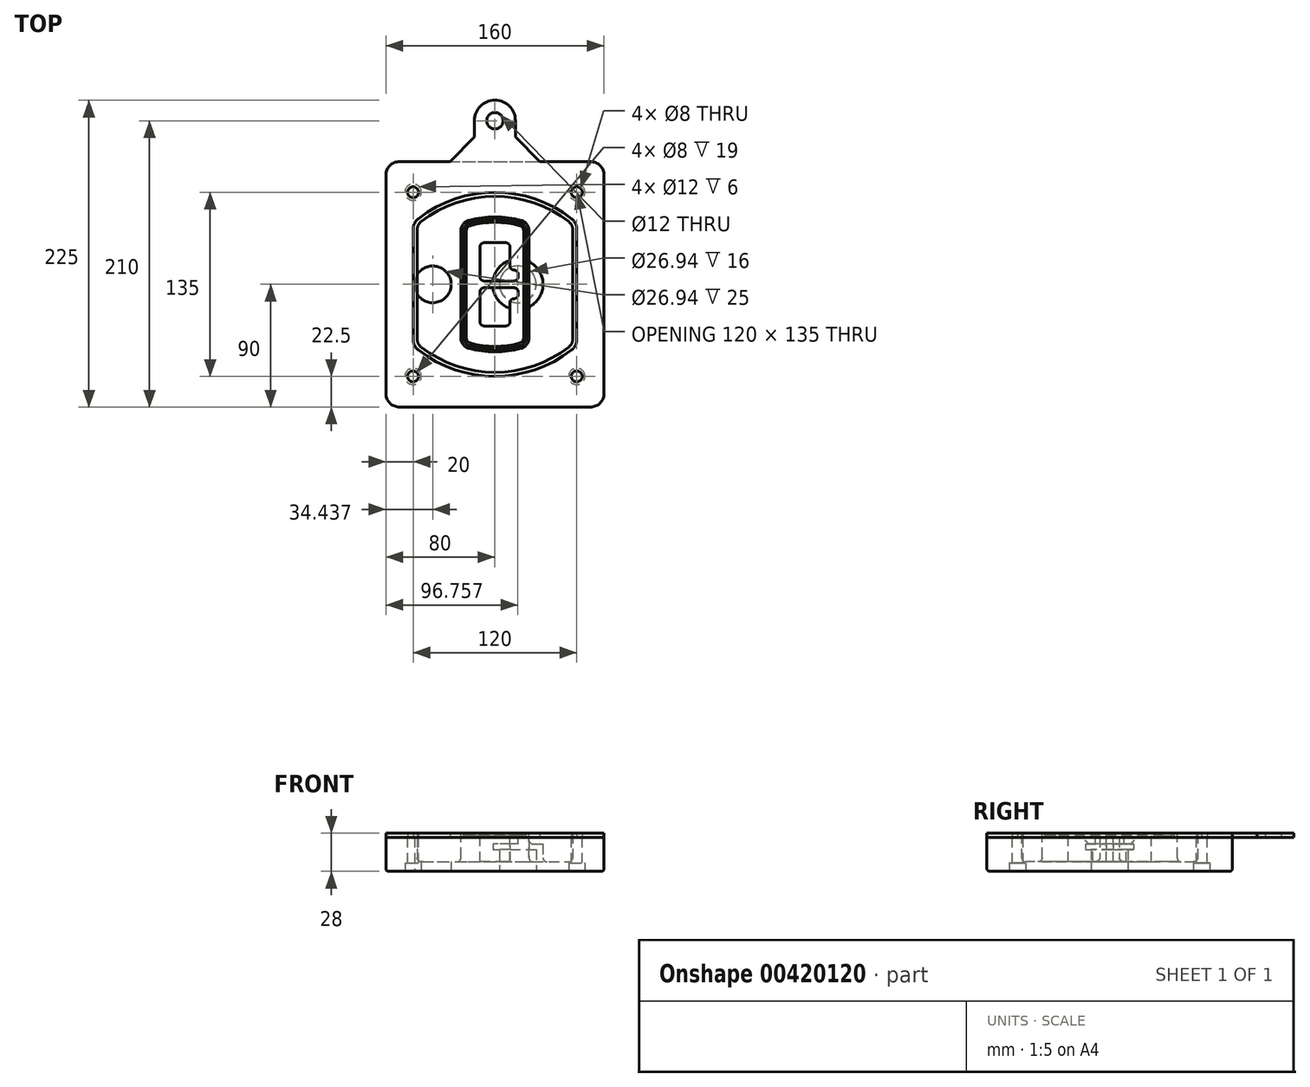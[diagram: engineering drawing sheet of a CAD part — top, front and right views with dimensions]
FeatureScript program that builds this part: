
annotation { "Feature Type Name" : "Feature", "Feature Type Description" : "" }
export const myFeature = defineFeature(function(context is Context, id is Id, definition is map)
    precondition{}
    {
        {
            var Q0;
            Q0=qCreatedBy(makeId("Top.planeOp"),FACE);
            var sketch = newSketch(context, id + "F0", { "sketchPlane" : qUnion([Q0])});
            skPoint(sketch, "E0.rect.middle", {"position": v(0, 0) * mm});
            skLineSegment(sketch, "E1.bottom", {"start": v(-70, -90) * mm, "end": v(70, -90) * mm});
            skLineSegment(sketch, "E1.top", {"start": v(-70, 90) * mm, "end": v(70, 90) * mm});
            skLineSegment(sketch, "E1.left", {"start": v(-80, -80) * mm, "end": v(-80, 80) * mm});
            skLineSegment(sketch, "E1.right", {"start": v(80, -80) * mm, "end": v(80, 80) * mm});
            skLineSegment(sketch, "E2", {"start": v(-80, 90) * mm, "end": v(80, -90) * mm, "construction": true});
            skLineSegment(sketch, "E3", {"start": v(80, 90) * mm, "end": v(-80, -90) * mm, "construction": true});
            skCircle(sketch, "E4", {"center": v(-60, 67.5) * mm, "radius": 4 * mm});
            skCircle(sketch, "E5", {"center": v(60, 67.5) * mm, "radius": 4 * mm});
            skCircle(sketch, "E6", {"center": v(60, -67.5) * mm, "radius": 4 * mm});
            skCircle(sketch, "E7", {"center": v(-60, -67.5) * mm, "radius": 4 * mm});
            skLineSegment(sketch, "E8", {"start": v(-60, 67.5) * mm, "end": v(60, 67.5) * mm, "construction": true});
            skLineSegment(sketch, "E9", {"start": v(60, 67.5) * mm, "end": v(60, -67.5) * mm, "construction": true});
            skLineSegment(sketch, "E10", {"start": v(60, -67.5) * mm, "end": v(-60, -67.5) * mm, "construction": true});
            skLineSegment(sketch, "E11", {"start": v(-60, -67.5) * mm, "end": v(-60, 67.5) * mm, "construction": true});
            skLineSegment(sketch, "E12", {"start": v(-60, 40.3) * mm, "end": v(-60, -40.3) * mm});
            skLineSegment(sketch, "E13", {"start": v(60, 40.3) * mm, "end": v(60, -40.3) * mm});
            skArc(sketch, "E14", {"start": v(56.15, 48.18) * mm, "mid": v(0, 67.5) * mm, "end": v(-56.15, 48.18) * mm});
            skArc(sketch, "E15", {"start": v(-56.15, -48.18) * mm, "mid": v(0, -67.5) * mm, "end": v(56.15, -48.18) * mm});
            skLineSegment(sketch, "E16", {"start": v(-60, 0) * mm, "end": v(60, 0) * mm, "construction": true});
            skPoint(sketch, "E17.visualSharp", {"position": v(-60, -45) * mm});
            skArc(sketch, "E17.filletArc", {"start": v(-60, -40.3) * mm, "mid": v(-58.99, -44.68) * mm, "end": v(-56.15, -48.18) * mm});
            skPoint(sketch, "E18.visualSharp", {"position": v(-60, 45) * mm});
            skArc(sketch, "E18.filletArc", {"start": v(-56.15, 48.18) * mm, "mid": v(-58.99, 44.68) * mm, "end": v(-60, 40.3) * mm});
            skPoint(sketch, "E19.visualSharp", {"position": v(60, 45) * mm});
            skArc(sketch, "E19.filletArc", {"start": v(60, 40.3) * mm, "mid": v(58.99, 44.68) * mm, "end": v(56.15, 48.18) * mm});
            skPoint(sketch, "E20.visualSharp", {"position": v(60, -45) * mm});
            skArc(sketch, "E20.filletArc", {"start": v(56.15, -48.18) * mm, "mid": v(58.99, -44.68) * mm, "end": v(60, -40.3) * mm});
            skPoint(sketch, "E21.visualSharp", {"position": v(-80, 90) * mm});
            skArc(sketch, "E21.filletArc", {"start": v(-70, 90) * mm, "mid": v(-77.07, 87.07) * mm, "end": v(-80, 80) * mm});
            skPoint(sketch, "E22.visualSharp", {"position": v(80, 90) * mm});
            skArc(sketch, "E22.filletArc", {"start": v(80, 80) * mm, "mid": v(77.07, 87.07) * mm, "end": v(70, 90) * mm});
            skPoint(sketch, "E23.visualSharp", {"position": v(80, -90) * mm});
            skArc(sketch, "E23.filletArc", {"start": v(70, -90) * mm, "mid": v(77.07, -87.07) * mm, "end": v(80, -80) * mm});
            skPoint(sketch, "E24.visualSharp", {"position": v(-80, -90) * mm});
            skArc(sketch, "E24.filletArc", {"start": v(-80, -80) * mm, "mid": v(-77.07, -87.07) * mm, "end": v(-70, -90) * mm});
            skArc(sketch, "E25.0", {"start": v(57, 40.3) * mm, "mid": v(56.3, 43.36) * mm, "end": v(54.3, 45.81) * mm});
            skLineSegment(sketch, "E25.1", {"start": v(57, 40.3) * mm, "end": v(57, -40.3) * mm});
            skArc(sketch, "E25.2", {"start": v(54.3, -45.81) * mm, "mid": v(56.3, -43.36) * mm, "end": v(57, -40.3) * mm});
            skArc(sketch, "E25.3", {"start": v(-54.3, -45.81) * mm, "mid": v(0, -64.5) * mm, "end": v(54.3, -45.81) * mm});
            skArc(sketch, "E25.4", {"start": v(-57, -40.3) * mm, "mid": v(-56.3, -43.36) * mm, "end": v(-54.3, -45.81) * mm});
            skArc(sketch, "E25.5", {"start": v(54.3, 45.81) * mm, "mid": v(0, 64.5) * mm, "end": v(-54.3, 45.81) * mm});
            skLineSegment(sketch, "E25.6", {"start": v(-57, 40.3) * mm, "end": v(-57, -40.3) * mm});
            skArc(sketch, "E25.7", {"start": v(-54.3, 45.81) * mm, "mid": v(-56.3, 43.36) * mm, "end": v(-57, 40.3) * mm});
            skArc(sketch, "E26.0", {"start": v(-58.62, 51.33) * mm, "mid": v(-62.58, 46.43) * mm, "end": v(-64, 40.3) * mm});
            skArc(sketch, "E26.1", {"start": v(58.62, 51.33) * mm, "mid": v(0, 71.5) * mm, "end": v(-58.62, 51.33) * mm});
            skArc(sketch, "E26.2", {"start": v(64, 40.3) * mm, "mid": v(62.58, 46.43) * mm, "end": v(58.62, 51.33) * mm});
            skLineSegment(sketch, "E26.3", {"start": v(64, 40.3) * mm, "end": v(64, -40.3) * mm});
            skArc(sketch, "E26.4", {"start": v(58.62, -51.33) * mm, "mid": v(62.58, -46.43) * mm, "end": v(64, -40.3) * mm});
            skLineSegment(sketch, "E26.5", {"start": v(-64, 40.3) * mm, "end": v(-64, -40.3) * mm});
            skArc(sketch, "E26.6", {"start": v(-58.62, -51.33) * mm, "mid": v(0, -71.5) * mm, "end": v(58.62, -51.33) * mm});
            skArc(sketch, "E26.7", {"start": v(-64, -40.3) * mm, "mid": v(-62.58, -46.43) * mm, "end": v(-58.62, -51.33) * mm});
            skSolve(sketch);
        }
        {
            var Q0;
            Q0=makeQuery(id+"F0.imprint","IMPRINT",FACE,{"disambiguationData":[TD([[makeQuery(id+"F0.imprint","IMPRINT",EDGE,{"derivedFrom":sQuery(id+"F0.wireOp",EDGE,"E1.bottom")}),1.0]])]});
            var Q1;
            Q1=makeQuery(id+"F0.imprint","IMPRINT",FACE,{"disambiguationData":[TD([[makeQuery(id+"F0.imprint","IMPRINT",EDGE,{"derivedFrom":sQuery(id+"F0.wireOp",EDGE,"E12")}),1.0]])]});
            var Q2;
            Q2=makeQuery(id+"F0.imprint","IMPRINT",FACE,{"disambiguationData":[TD([[makeQuery(id+"F0.imprint","IMPRINT",EDGE,{"derivedFrom":sQuery(id+"F0.wireOp",EDGE,"E25.0")}),1.0]])]});
            var Q3;
            Q3=makeQuery(id+"F0.imprint","IMPRINT",FACE,{"disambiguationData":[TD([[makeQuery(id+"F0.imprint","IMPRINT",EDGE,{"derivedFrom":sQuery(id+"F0.wireOp",EDGE,"E12")}),-1.0]])]});
            extrude(context, id + "F1", {"entities" : qUnion([Q0, Q1, Q2, Q3]), "oppositeDirection" : true, "depth" : 25 * mm});
        }
        {
            var Q0;
            Q0=makeQuery(id+"F0.imprint","IMPRINT",FACE,{"disambiguationData":[TD([[makeQuery(id+"F0.imprint","IMPRINT",EDGE,{"derivedFrom":sQuery(id+"F0.wireOp",EDGE,"E12")}),1.0]])]});
            extrude(context, id + "F2", {"entities" : qUnion([Q0]), "operationType" : NewBodyOperationType.ADD, "depth" : 3 * mm});
        }
        {
            var Q0;
            Q0=makeQuery(id+"F0.imprint","IMPRINT",FACE,{"disambiguationData":[TD([[makeQuery(id+"F0.imprint","IMPRINT",EDGE,{"derivedFrom":sQuery(id+"F0.wireOp",EDGE,"E25.0")}),1.0]])]});
            extrude(context, id + "F3", {"entities" : qUnion([Q0]), "operationType" : NewBodyOperationType.REMOVE, "oppositeDirection" : true, "depth" : 18 * mm});
        }
        {
            var Q0;
            Q0=makeQuery(id+"F2.opExtrude","CAP_FACE",FACE,{"disambiguationData":[OSD([sQuery(id+"F0.wireOp",EDGE,"E12"),sQuery(id+"F0.wireOp",EDGE,"E13"),sQuery(id+"F0.wireOp",EDGE,"E14"),sQuery(id+"F0.wireOp",EDGE,"E15"),sQuery(id+"F0.wireOp",EDGE,"E17.filletArc"),sQuery(id+"F0.wireOp",EDGE,"E18.filletArc"),sQuery(id+"F0.wireOp",EDGE,"E19.filletArc"),sQuery(id+"F0.wireOp",EDGE,"E20.filletArc"),sQuery(id+"F0.wireOp",EDGE,"E25.0"),sQuery(id+"F0.wireOp",EDGE,"E25.1"),sQuery(id+"F0.wireOp",EDGE,"E25.2"),sQuery(id+"F0.wireOp",EDGE,"E25.3"),sQuery(id+"F0.wireOp",EDGE,"E25.4"),sQuery(id+"F0.wireOp",EDGE,"E25.5"),sQuery(id+"F0.wireOp",EDGE,"E25.6"),sQuery(id+"F0.wireOp",EDGE,"E25.7")])],"isStart":false});
            var sketch = newSketch(context, id + "F4", { "sketchPlane" : qUnion([Q0])});
            skArc(sketch, "E27.0", {"start": v(-19.08, -46.97) * mm, "mid": v(0, -49.5) * mm, "end": v(19.08, -46.97) * mm});
            skArc(sketch, "E28.0", {"start": v(19.08, 46.97) * mm, "mid": v(0, 49.5) * mm, "end": v(-19.08, 46.97) * mm});
            skLineSegment(sketch, "E29", {"start": v(-25, 39.25) * mm, "end": v(-25, -39.25) * mm});
            skLineSegment(sketch, "E30", {"start": v(25, 39.25) * mm, "end": v(25, -39.25) * mm});
            skLineSegment(sketch, "E31", {"start": v(-25, 45.1) * mm, "end": v(25, 45.1) * mm, "construction": true});
            skLineSegment(sketch, "E32", {"start": v(-25, -45.1) * mm, "end": v(25, -45.1) * mm, "construction": true});
            skPoint(sketch, "E33.visualSharp", {"position": v(-25, 45.1) * mm});
            skArc(sketch, "E33.filletArc", {"start": v(-19.08, 46.97) * mm, "mid": v(-23.35, 44.11) * mm, "end": v(-25, 39.25) * mm});
            skPoint(sketch, "E34.visualSharp", {"position": v(25, 45.1) * mm});
            skArc(sketch, "E34.filletArc", {"start": v(25, 39.25) * mm, "mid": v(23.35, 44.11) * mm, "end": v(19.08, 46.97) * mm});
            skPoint(sketch, "E35.visualSharp", {"position": v(25, -45.1) * mm});
            skArc(sketch, "E35.filletArc", {"start": v(19.08, -46.97) * mm, "mid": v(23.35, -44.11) * mm, "end": v(25, -39.25) * mm});
            skPoint(sketch, "E36.visualSharp", {"position": v(-25, -45.1) * mm});
            skArc(sketch, "E36.filletArc", {"start": v(-25, -39.25) * mm, "mid": v(-23.35, -44.11) * mm, "end": v(-19.08, -46.97) * mm});
            skArc(sketch, "E37.0", {"start": v(54.3, 45.81) * mm, "mid": v(0, 64.5) * mm, "end": v(-54.3, 45.81) * mm});
            skArc(sketch, "E37.1", {"start": v(-54.3, 45.81) * mm, "mid": v(-56.3, 43.36) * mm, "end": v(-57, 40.3) * mm});
            skLineSegment(sketch, "E37.2", {"start": v(-57, 40.3) * mm, "end": v(-57, -40.3) * mm});
            skArc(sketch, "E37.3", {"start": v(-57, -40.3) * mm, "mid": v(-56.3, -43.36) * mm, "end": v(-54.3, -45.81) * mm});
            skArc(sketch, "E37.4", {"start": v(-54.3, -45.81) * mm, "mid": v(0, -64.5) * mm, "end": v(54.3, -45.81) * mm});
            skArc(sketch, "E37.5", {"start": v(54.3, -45.81) * mm, "mid": v(56.3, -43.36) * mm, "end": v(57, -40.3) * mm});
            skLineSegment(sketch, "E37.6", {"start": v(57, 40.3) * mm, "end": v(57, -40.3) * mm});
            skArc(sketch, "E37.7", {"start": v(57, 40.3) * mm, "mid": v(56.3, 43.36) * mm, "end": v(54.3, 45.81) * mm});
            skLineSegment(sketch, "E38.0", {"start": v(23, 39.25) * mm, "end": v(23, -39.25) * mm});
            skArc(sketch, "E38.1", {"start": v(18.56, -45.04) * mm, "mid": v(21.76, -42.9) * mm, "end": v(23, -39.25) * mm});
            skArc(sketch, "E38.2", {"start": v(-18.56, -45.04) * mm, "mid": v(0, -47.5) * mm, "end": v(18.56, -45.04) * mm});
            skArc(sketch, "E38.3", {"start": v(-23, -39.25) * mm, "mid": v(-21.76, -42.9) * mm, "end": v(-18.56, -45.04) * mm});
            skLineSegment(sketch, "E38.4", {"start": v(-23, 39.25) * mm, "end": v(-23, -39.25) * mm});
            skArc(sketch, "E38.5", {"start": v(23, 39.25) * mm, "mid": v(21.76, 42.9) * mm, "end": v(18.56, 45.04) * mm});
            skArc(sketch, "E38.6", {"start": v(-18.56, 45.04) * mm, "mid": v(-21.76, 42.9) * mm, "end": v(-23, 39.25) * mm});
            skArc(sketch, "E38.7", {"start": v(18.56, 45.04) * mm, "mid": v(0, 47.5) * mm, "end": v(-18.56, 45.04) * mm});
            skArc(sketch, "E39.0", {"start": v(21, 39.25) * mm, "mid": v(20.18, 41.68) * mm, "end": v(18.04, 43.1) * mm});
            skLineSegment(sketch, "E39.1", {"start": v(21, 39.25) * mm, "end": v(21, -39.25) * mm});
            skArc(sketch, "E39.2", {"start": v(18.04, -43.1) * mm, "mid": v(20.18, -41.68) * mm, "end": v(21, -39.25) * mm});
            skArc(sketch, "E39.3", {"start": v(-18.04, -43.1) * mm, "mid": v(0, -45.5) * mm, "end": v(18.04, -43.1) * mm});
            skArc(sketch, "E39.4", {"start": v(-21, -39.25) * mm, "mid": v(-20.18, -41.68) * mm, "end": v(-18.04, -43.1) * mm});
            skArc(sketch, "E39.5", {"start": v(18.04, 43.1) * mm, "mid": v(0, 45.5) * mm, "end": v(-18.04, 43.1) * mm});
            skLineSegment(sketch, "E39.6", {"start": v(-21, 39.25) * mm, "end": v(-21, -39.25) * mm});
            skArc(sketch, "E39.7", {"start": v(-18.04, 43.1) * mm, "mid": v(-20.18, 41.68) * mm, "end": v(-21, 39.25) * mm});
            skLineSegment(sketch, "E40", {"start": v(-25, 0) * mm, "end": v(25, 0) * mm, "construction": true});
            skLineSegment(sketch, "E41", {"start": v(-11, 5.5) * mm, "end": v(-11, 27.5) * mm});
            skLineSegment(sketch, "E42", {"start": v(-8, 30.5) * mm, "end": v(8, 30.5) * mm});
            skLineSegment(sketch, "E43", {"start": v(11, 27.5) * mm, "end": v(11, 13.5) * mm});
            skLineSegment(sketch, "E44", {"start": v(14, 10.5) * mm, "end": v(14, 10.5) * mm});
            skLineSegment(sketch, "E45", {"start": v(17, 7.5) * mm, "end": v(17, 5.5) * mm});
            skLineSegment(sketch, "E46", {"start": v(14, 2.5) * mm, "end": v(-8, 2.5) * mm});
            skPoint(sketch, "E47.visualSharp", {"position": v(-11, 30.5) * mm});
            skArc(sketch, "E47.filletArc", {"start": v(-8, 30.5) * mm, "mid": v(-10.12, 29.62) * mm, "end": v(-11, 27.5) * mm});
            skPoint(sketch, "E48.visualSharp", {"position": v(11, 30.5) * mm});
            skArc(sketch, "E48.filletArc", {"start": v(11, 27.5) * mm, "mid": v(10.12, 29.62) * mm, "end": v(8, 30.5) * mm});
            skPoint(sketch, "E49.visualSharp", {"position": v(11, 10.5) * mm});
            skArc(sketch, "E49.filletArc", {"start": v(11, 13.5) * mm, "mid": v(11.88, 11.38) * mm, "end": v(14, 10.5) * mm});
            skPoint(sketch, "E50.visualSharp", {"position": v(17, 10.5) * mm});
            skArc(sketch, "E50.filletArc", {"start": v(17, 7.5) * mm, "mid": v(16.12, 9.62) * mm, "end": v(14, 10.5) * mm});
            skPoint(sketch, "E51.visualSharp", {"position": v(17, 2.5) * mm});
            skArc(sketch, "E51.filletArc", {"start": v(14, 2.5) * mm, "mid": v(16.12, 3.38) * mm, "end": v(17, 5.5) * mm});
            skPoint(sketch, "E52.visualSharp", {"position": v(-11, 2.5) * mm});
            skArc(sketch, "E52.filletArc", {"start": v(-11, 5.5) * mm, "mid": v(-10.12, 3.38) * mm, "end": v(-8, 2.5) * mm});
            skLineSegment(sketch, "E53.0.MirrorCS", {"start": v(14, -2.5) * mm, "end": v(-8, -2.5) * mm});
            skArc(sketch, "E54.0.MirrorCS", {"start": v(-11, -5.5) * mm, "mid": v(-10.12, -3.38) * mm, "end": v(-8, -2.5) * mm});
            skLineSegment(sketch, "E55.0.MirrorCS", {"start": v(-11, -5.5) * mm, "end": v(-11, -27.5) * mm});
            skArc(sketch, "E56.0.MirrorCS", {"start": v(-8, -30.5) * mm, "mid": v(-10.12, -29.62) * mm, "end": v(-11, -27.5) * mm});
            skLineSegment(sketch, "E57.0.MirrorCS", {"start": v(-8, -30.5) * mm, "end": v(8, -30.5) * mm});
            skArc(sketch, "E58.0.MirrorCS", {"start": v(11, -27.5) * mm, "mid": v(10.12, -29.62) * mm, "end": v(8, -30.5) * mm});
            skLineSegment(sketch, "E59.0.MirrorCS", {"start": v(11, -27.5) * mm, "end": v(11, -13.5) * mm});
            skArc(sketch, "E60.0.MirrorCS", {"start": v(11, -13.5) * mm, "mid": v(11.88, -11.38) * mm, "end": v(14, -10.5) * mm});
            skArc(sketch, "E61.0.MirrorCS", {"start": v(17, -7.5) * mm, "mid": v(16.12, -9.62) * mm, "end": v(14, -10.5) * mm});
            skLineSegment(sketch, "E62.0.MirrorCS", {"start": v(17, -7.5) * mm, "end": v(17, -5.5) * mm});
            skArc(sketch, "E63.0.MirrorCS", {"start": v(14, -2.5) * mm, "mid": v(16.12, -3.38) * mm, "end": v(17, -5.5) * mm});
            skSolve(sketch);
        }
        {
            var Q0;
            Q0=makeQuery(id+"F4.imprint","IMPRINT",FACE,{"disambiguationData":[TD([[makeQuery(id+"F4.imprint","IMPRINT",EDGE,{"derivedFrom":sQuery(id+"F4.wireOp",EDGE,"E27.0")}),1.0]])]});
            var Q1;
            Q1=makeQuery(id+"F4.imprint","IMPRINT",FACE,{"disambiguationData":[TD([[makeQuery(id+"F4.imprint","IMPRINT",EDGE,{"derivedFrom":sQuery(id+"F4.wireOp",EDGE,"E38.0")}),-1.0]])]});
            var Q2;
            Q2=makeQuery(id+"F4.imprint","IMPRINT",FACE,{"disambiguationData":[TD([[makeQuery(id+"F4.imprint","IMPRINT",EDGE,{"derivedFrom":sQuery(id+"F4.wireOp",EDGE,"E39.0")}),1.0]])]});
            extrude(context, id + "F5", {"entities" : qUnion([Q0, Q1, Q2]), "operationType" : NewBodyOperationType.ADD, "endBound" : BoundingType.UP_TO_NEXT, "oppositeDirection" : true, "depth" : 25 * mm});
        }
        {
            var Q0;
            Q0=makeQuery(id+"F4.imprint","IMPRINT",FACE,{"disambiguationData":[TD([[makeQuery(id+"F4.imprint","IMPRINT",EDGE,{"derivedFrom":sQuery(id+"F4.wireOp",EDGE,"E38.0")}),-1.0]])]});
            extrude(context, id + "F6", {"entities" : qUnion([Q0]), "operationType" : NewBodyOperationType.REMOVE, "oppositeDirection" : true, "depth" : 2 * mm});
        }
        {
            var Q0;
            Q0=makeQuery(id+"F1.opExtrude","CAP_FACE",FACE,{"disambiguationData":[OSD([sQuery(id+"F0.wireOp",EDGE,"E1.bottom"),sQuery(id+"F0.wireOp",EDGE,"E1.top"),sQuery(id+"F0.wireOp",EDGE,"E1.left"),sQuery(id+"F0.wireOp",EDGE,"E1.right"),sQuery(id+"F0.wireOp",EDGE,"E4"),sQuery(id+"F0.wireOp",EDGE,"E5"),sQuery(id+"F0.wireOp",EDGE,"E6"),sQuery(id+"F0.wireOp",EDGE,"E7"),sQuery(id+"F0.wireOp",EDGE,"E21.filletArc"),sQuery(id+"F0.wireOp",EDGE,"E22.filletArc"),sQuery(id+"F0.wireOp",EDGE,"E23.filletArc"),sQuery(id+"F0.wireOp",EDGE,"E24.filletArc")])],"isStart":false});
            var sketch = newSketch(context, id + "F7", { "sketchPlane" : qUnion([Q0])});
            skCircle(sketch, "E64", {"center": v(16.76, 0) * mm, "radius": 13.47 * mm});
            skCircle(sketch, "E65", {"center": v(-45.56, 0) * mm, "radius": 13.47 * mm});
            skLineSegment(sketch, "E66", {"start": v(80, 0) * mm, "end": v(-80, 0) * mm});
            skCircle(sketch, "E67", {"center": v(16.76, 0) * mm, "radius": 18.47 * mm});
            skCircle(sketch, "E68", {"center": v(60, -67.5) * mm, "radius": 6 * mm});
            skCircle(sketch, "E69", {"center": v(-60, -67.5) * mm, "radius": 6 * mm});
            skCircle(sketch, "E70", {"center": v(-60, 67.5) * mm, "radius": 6 * mm});
            skCircle(sketch, "E71", {"center": v(60, 67.5) * mm, "radius": 6 * mm});
            skSolve(sketch);
        }
        {
            var Q0;
            {var subQ1=sQuery(id+"F7.wireOp",EDGE,"E66");var subQ4=sQuery(id+"F7.wireOp",EDGE,"E64");var subQ6=makeQuery(id+"F7.imprint","INTERSECT",VERTEX,{"disambiguationData":[OD(0.0)],"derivedFrom":[subQ4,subQ1]});Q0=makeQuery(id+"F7.imprint","IMPRINT",FACE,{"disambiguationData":[TD([[makeQuery(id+"F7.imprint","IMPRINT",EDGE,{"disambiguationData":[TD([[subQ6,-1.0]])],"derivedFrom":subQ4}),-1.0]])]});}
            var Q1;
            {var subQ0=sQuery(id+"F7.wireOp",EDGE,"E66");var subQ1=sQuery(id+"F7.wireOp",EDGE,"E64");var subQ3=makeQuery(id+"F7.imprint","INTERSECT",VERTEX,{"disambiguationData":[OD(0.0)],"derivedFrom":[subQ1,subQ0]});Q1=makeQuery(id+"F7.imprint","IMPRINT",FACE,{"disambiguationData":[TD([[makeQuery(id+"F7.imprint","IMPRINT",EDGE,{"disambiguationData":[TD([[subQ3,-1.0]])],"derivedFrom":subQ1}),1.0]])]});}
            var Q2;
            {var subQ0=sQuery(id+"F7.wireOp",EDGE,"E66");var subQ1=sQuery(id+"F7.wireOp",EDGE,"E64");var subQ3=makeQuery(id+"F7.imprint","INTERSECT",VERTEX,{"disambiguationData":[OD(0.0)],"derivedFrom":[subQ1,subQ0]});Q2=makeQuery(id+"F7.imprint","IMPRINT",FACE,{"disambiguationData":[TD([[makeQuery(id+"F7.imprint","IMPRINT",EDGE,{"disambiguationData":[TD([[subQ3,1.0]])],"derivedFrom":subQ1}),1.0]])]});}
            var Q3;
            {var subQ1=sQuery(id+"F7.wireOp",EDGE,"E66");var subQ4=sQuery(id+"F7.wireOp",EDGE,"E64");var subQ6=makeQuery(id+"F7.imprint","INTERSECT",VERTEX,{"disambiguationData":[OD(0.0)],"derivedFrom":[subQ4,subQ1]});Q3=makeQuery(id+"F7.imprint","IMPRINT",FACE,{"disambiguationData":[TD([[makeQuery(id+"F7.imprint","IMPRINT",EDGE,{"disambiguationData":[TD([[subQ6,1.0]])],"derivedFrom":subQ4}),-1.0]])]});}
            extrude(context, id + "F8", {"entities" : qUnion([Q0, Q1, Q2, Q3]), "operationType" : NewBodyOperationType.ADD, "oppositeDirection" : true, "depth" : 20 * mm});
        }
        {
            var Q0;
            {var subQ0=sQuery(id+"F7.wireOp",EDGE,"E66");var subQ1=sQuery(id+"F7.wireOp",EDGE,"E64");var subQ3=makeQuery(id+"F7.imprint","INTERSECT",VERTEX,{"disambiguationData":[OD(0.0)],"derivedFrom":[subQ1,subQ0]});Q0=makeQuery(id+"F7.imprint","IMPRINT",FACE,{"disambiguationData":[TD([[makeQuery(id+"F7.imprint","IMPRINT",EDGE,{"disambiguationData":[TD([[subQ3,-1.0]])],"derivedFrom":subQ1}),1.0]])]});}
            var Q1;
            {var subQ0=sQuery(id+"F7.wireOp",EDGE,"E66");var subQ1=sQuery(id+"F7.wireOp",EDGE,"E64");var subQ3=makeQuery(id+"F7.imprint","INTERSECT",VERTEX,{"disambiguationData":[OD(0.0)],"derivedFrom":[subQ1,subQ0]});Q1=makeQuery(id+"F7.imprint","IMPRINT",FACE,{"disambiguationData":[TD([[makeQuery(id+"F7.imprint","IMPRINT",EDGE,{"disambiguationData":[TD([[subQ3,1.0]])],"derivedFrom":subQ1}),1.0]])]});}
            extrude(context, id + "F9", {"entities" : qUnion([Q0, Q1]), "operationType" : NewBodyOperationType.REMOVE, "oppositeDirection" : true, "depth" : 16 * mm});
        }
        {
            var Q0;
            {var subQ0=sQuery(id+"F7.wireOp",EDGE,"E66");var subQ1=sQuery(id+"F7.wireOp",EDGE,"E65");var subQ3=makeQuery(id+"F7.imprint","INTERSECT",VERTEX,{"disambiguationData":[OD(0.0)],"derivedFrom":[subQ1,subQ0]});Q0=makeQuery(id+"F7.imprint","IMPRINT",FACE,{"disambiguationData":[TD([[makeQuery(id+"F7.imprint","IMPRINT",EDGE,{"disambiguationData":[TD([[subQ3,-1.0]])],"derivedFrom":subQ1}),1.0]])]});}
            var Q1;
            {var subQ0=sQuery(id+"F7.wireOp",EDGE,"E66");var subQ1=sQuery(id+"F7.wireOp",EDGE,"E65");var subQ3=makeQuery(id+"F7.imprint","INTERSECT",VERTEX,{"disambiguationData":[OD(0.0)],"derivedFrom":[subQ1,subQ0]});Q1=makeQuery(id+"F7.imprint","IMPRINT",FACE,{"disambiguationData":[TD([[makeQuery(id+"F7.imprint","IMPRINT",EDGE,{"disambiguationData":[TD([[subQ3,1.0]])],"derivedFrom":subQ1}),1.0]])]});}
            extrude(context, id + "F10", {"entities" : qUnion([Q0, Q1]), "operationType" : NewBodyOperationType.REMOVE, "oppositeDirection" : true, "depth" : 25 * mm});
        }
        {
            var Q0;
            Q0=makeQuery(id+"F7.imprint","IMPRINT",FACE,{"disambiguationData":[TD([[makeQuery(id+"F7.imprint","IMPRINT",EDGE,{"derivedFrom":sQuery(id+"F7.wireOp",EDGE,"E68")}),1.0]])]});
            var Q1;
            Q1=makeQuery(id+"F7.imprint","IMPRINT",FACE,{"disambiguationData":[TD([[makeQuery(id+"F7.imprint","IMPRINT",EDGE,{"derivedFrom":makeQuery(id+"F1.opExtrude","CAP_EDGE",EDGE,{"disambiguationData":[OSD([sQuery(id+"F0.wireOp",EDGE,"E5")])],"isStart":false})}),-1.0]])]});
            var Q2;
            Q2=makeQuery(id+"F7.imprint","IMPRINT",FACE,{"disambiguationData":[TD([[makeQuery(id+"F7.imprint","IMPRINT",EDGE,{"derivedFrom":sQuery(id+"F7.wireOp",EDGE,"E69")}),1.0]])]});
            var Q3;
            Q3=makeQuery(id+"F7.imprint","IMPRINT",FACE,{"disambiguationData":[TD([[makeQuery(id+"F7.imprint","IMPRINT",EDGE,{"derivedFrom":makeQuery(id+"F1.opExtrude","CAP_EDGE",EDGE,{"disambiguationData":[OSD([sQuery(id+"F0.wireOp",EDGE,"E4")])],"isStart":false})}),-1.0]])]});
            var Q4;
            Q4=makeQuery(id+"F7.imprint","IMPRINT",FACE,{"disambiguationData":[TD([[makeQuery(id+"F7.imprint","IMPRINT",EDGE,{"derivedFrom":sQuery(id+"F7.wireOp",EDGE,"E70")}),1.0]])]});
            var Q5;
            Q5=makeQuery(id+"F7.imprint","IMPRINT",FACE,{"disambiguationData":[TD([[makeQuery(id+"F7.imprint","IMPRINT",EDGE,{"derivedFrom":makeQuery(id+"F1.opExtrude","CAP_EDGE",EDGE,{"disambiguationData":[OSD([sQuery(id+"F0.wireOp",EDGE,"E7")])],"isStart":false})}),-1.0]])]});
            var Q6;
            Q6=makeQuery(id+"F7.imprint","IMPRINT",FACE,{"disambiguationData":[TD([[makeQuery(id+"F7.imprint","IMPRINT",EDGE,{"derivedFrom":sQuery(id+"F7.wireOp",EDGE,"E71")}),1.0]])]});
            var Q7;
            Q7=makeQuery(id+"F7.imprint","IMPRINT",FACE,{"disambiguationData":[TD([[makeQuery(id+"F7.imprint","IMPRINT",EDGE,{"derivedFrom":makeQuery(id+"F1.opExtrude","CAP_EDGE",EDGE,{"disambiguationData":[OSD([sQuery(id+"F0.wireOp",EDGE,"E6")])],"isStart":false})}),-1.0]])]});
            extrude(context, id + "F11", {"entities" : qUnion([Q0, Q1, Q2, Q3, Q4, Q5, Q6, Q7]), "operationType" : NewBodyOperationType.REMOVE, "oppositeDirection" : true, "depth" : 6 * mm});
        }
        {
            var Q0;
            Q0=makeQuery(id+"F9.boolean.opBoolean","COPY",FACE,{"derivedFrom":makeQuery(id+"F9.opExtrude","CAP_FACE",FACE,{"disambiguationData":[OSD([sQuery(id+"F7.wireOp",EDGE,"E64")])],"isStart":false})});
            var sketch = newSketch(context, id + "F12", { "sketchPlane" : qUnion([Q0])});
            skArc(sketch, "E72.0", {"start": v(11, 17.55) * mm, "mid": v(2.57, 11.82) * mm, "end": v(-1.54, 2.5) * mm});
            skArc(sketch, "E72.1", {"start": v(-1.54, -2.5) * mm, "mid": v(2.57, -11.82) * mm, "end": v(11, -17.55) * mm});
            skLineSegment(sketch, "E73", {"start": v(-1.54, -2.5) * mm, "end": v(14, -2.5) * mm});
            skLineSegment(sketch, "E74.0", {"start": v(14, 2.5) * mm, "end": v(-1.54, 2.5) * mm});
            skArc(sketch, "E74.1", {"start": v(14, 2.5) * mm, "mid": v(16.12, 3.38) * mm, "end": v(17, 5.5) * mm});
            skLineSegment(sketch, "E74.2", {"start": v(17, 7.5) * mm, "end": v(17, 5.5) * mm});
            skArc(sketch, "E74.3", {"start": v(17, 7.5) * mm, "mid": v(16.12, 9.62) * mm, "end": v(14, 10.5) * mm});
            skArc(sketch, "E74.4", {"start": v(11, 13.5) * mm, "mid": v(11.88, 11.38) * mm, "end": v(14, 10.5) * mm});
            skLineSegment(sketch, "E74.5", {"start": v(11, 17.55) * mm, "end": v(11, 13.5) * mm});
            skLineSegment(sketch, "E74.7", {"start": v(14, -2.5) * mm, "end": v(-1.54, -2.5) * mm});
            skArc(sketch, "E74.8", {"start": v(14, -2.5) * mm, "mid": v(16.12, -3.38) * mm, "end": v(17, -5.5) * mm});
            skLineSegment(sketch, "E74.9", {"start": v(17, -7.5) * mm, "end": v(17, -5.5) * mm});
            skArc(sketch, "E74.10", {"start": v(17, -7.5) * mm, "mid": v(16.12, -9.62) * mm, "end": v(14, -10.5) * mm});
            skArc(sketch, "E74.11", {"start": v(11, -13.5) * mm, "mid": v(11.88, -11.38) * mm, "end": v(14, -10.5) * mm});
            skLineSegment(sketch, "E74.12", {"start": v(11, -17.55) * mm, "end": v(11, -13.5) * mm});
            skPoint(sketch, "E75.orphan", {"position": v(11, -27.5) * mm});
            skPoint(sketch, "E76.orphan", {"position": v(-8, -2.5) * mm});
            skPoint(sketch, "E77.orphan", {"position": v(-8, 2.5) * mm});
            skPoint(sketch, "E78.orphan", {"position": v(11, 27.5) * mm});
            skSolve(sketch);
        }
        {
            var Q0;
            {var subQ7=sQuery(id+"F12.wireOp",EDGE,"E72.0");var subQ14=sQuery(id+"F12.wireOp",EDGE,"E72.1");var subQ16=sQuery(id+"F12.wireOp",EDGE,"E74.1");var subQ18=sQuery(id+"F12.wireOp",EDGE,"E74.8");Q0=qUnion([makeQuery(id+"F12.imprint","IMPRINT",FACE,{"disambiguationData":[TD([[makeQuery(id+"F12.imprint","IMPRINT",EDGE,{"derivedFrom":subQ7}),1.0]])]}),makeQuery(id+"F12.imprint","IMPRINT",FACE,{"disambiguationData":[TD([[makeQuery(id+"F12.imprint","IMPRINT",EDGE,{"derivedFrom":subQ14}),1.0]])]}),makeQuery(id+"F12.imprint","IMPRINT",FACE,{"disambiguationData":[TD([[makeQuery(id+"F12.imprint","IMPRINT",EDGE,{"derivedFrom":subQ16}),1.0]])]}),makeQuery(id+"F12.imprint","IMPRINT",FACE,{"disambiguationData":[TD([[makeQuery(id+"F12.imprint","IMPRINT",EDGE,{"derivedFrom":subQ18}),-1.0]])]})]);}
            var Q1;
            Q1=makeQuery(id+"F5.boolean.opBoolean","SPLIT",FACE,{"disambiguationData":[TD([makeQuery(id+"F5.opExtrude","SWEPT_FACE",FACE,{"disambiguationData":[OSD([sQuery(id+"F4.wireOp",EDGE,"E41")])]})])],"derivedFrom":makeQuery(id+"F3.boolean.opBoolean","COPY",FACE,{"derivedFrom":makeQuery(id+"F3.opExtrude","CAP_FACE",FACE,{"disambiguationData":[OSD([sQuery(id+"F0.wireOp",EDGE,"E25.0"),sQuery(id+"F0.wireOp",EDGE,"E25.1"),sQuery(id+"F0.wireOp",EDGE,"E25.2"),sQuery(id+"F0.wireOp",EDGE,"E25.3"),sQuery(id+"F0.wireOp",EDGE,"E25.4"),sQuery(id+"F0.wireOp",EDGE,"E25.5"),sQuery(id+"F0.wireOp",EDGE,"E25.6"),sQuery(id+"F0.wireOp",EDGE,"E25.7")])],"isStart":false})})});
            extrude(context, id + "F13", {"entities" : qUnion([Q0]), "operationType" : NewBodyOperationType.REMOVE, "endBound" : BoundingType.UP_TO_SURFACE, "endBoundEntityFace" : qUnion([Q1]), "depth" : 25 * mm});
        }
        {
            var Q0;
            Q0=makeQuery(id+"F3.boolean.opBoolean","COPY",EDGE,{"derivedFrom":makeQuery(id+"F3.opExtrude","CAP_EDGE",EDGE,{"disambiguationData":[OSD([sQuery(id+"F0.wireOp",EDGE,"E25.6")])],"isStart":false})});
            var Q1;
            Q1=makeQuery(id+"F8.boolean.opBoolean","INTERSECT",EDGE,{"derivedFrom":[makeQuery(id+"F5.opExtrude","SWEPT_FACE",FACE,{"disambiguationData":[OSD([sQuery(id+"F4.wireOp",EDGE,"E30")])]}),makeQuery(id+"F8.opExtrude","CAP_FACE",FACE,{"disambiguationData":[OSD([sQuery(id+"F7.wireOp",EDGE,"E67")])],"isStart":false})]});
            var Q2;
            Q2=makeQuery(id+"F8.boolean.opBoolean","INTERSECT",EDGE,{"disambiguationData":[OD(1.0)],"derivedFrom":[makeQuery(id+"F5.opExtrude","SWEPT_FACE",FACE,{"disambiguationData":[OSD([sQuery(id+"F4.wireOp",EDGE,"E30")])]}),makeQuery(id+"F8.opExtrude","SWEPT_FACE",FACE,{"disambiguationData":[OSD([sQuery(id+"F7.wireOp",EDGE,"E67")])]})]});
            var Q3;
            {var subQ0=sQuery(id+"F4.wireOp",EDGE,"E30");Q3=makeQuery(id+"F8.boolean.opBoolean","SPLIT",EDGE,{"disambiguationData":[TD([makeQuery(id+"F5.opExtrude","SWEPT_FACE",FACE,{"disambiguationData":[OSD([sQuery(id+"F4.wireOp",EDGE,"E35.filletArc")])]})])],"derivedFrom":makeQuery(id+"F5.opExtrude","CAP_EDGE",EDGE,{"disambiguationData":[OSD([subQ0])],"isStart":false})});}
            var Q4;
            {var subQ0=sQuery(id+"F0.wireOp",EDGE,"E25.7");var subQ1=sQuery(id+"F0.wireOp",EDGE,"E25.1");var subQ2=sQuery(id+"F0.wireOp",EDGE,"E25.6");var subQ3=sQuery(id+"F0.wireOp",EDGE,"E25.5");var subQ4=sQuery(id+"F0.wireOp",EDGE,"E25.4");var subQ5=sQuery(id+"F0.wireOp",EDGE,"E25.0");var subQ6=sQuery(id+"F0.wireOp",EDGE,"E25.2");var subQ7=sQuery(id+"F0.wireOp",EDGE,"E25.3");Q4=makeQuery(id+"F8.boolean.opBoolean","INTERSECT",EDGE,{"derivedFrom":[makeQuery(id+"F5.boolean.opBoolean","SPLIT",FACE,{"disambiguationData":[TD([makeQuery(id+"F2.opExtrude","SWEPT_FACE",FACE,{"disambiguationData":[OSD([subQ5])]})])],"derivedFrom":makeQuery(id+"F3.boolean.opBoolean","COPY",FACE,{"derivedFrom":makeQuery(id+"F3.opExtrude","CAP_FACE",FACE,{"disambiguationData":[OSD([subQ5,subQ1,subQ6,subQ7,subQ4,subQ3,subQ2,subQ0])],"isStart":false})})}),makeQuery(id+"F8.opExtrude","SWEPT_FACE",FACE,{"disambiguationData":[OSD([sQuery(id+"F7.wireOp",EDGE,"E67")])]})]});}
            var Q5;
            Q5=makeQuery(id+"F8.boolean.opBoolean","INTERSECT",EDGE,{"disambiguationData":[OD(0.0)],"derivedFrom":[makeQuery(id+"F5.opExtrude","SWEPT_FACE",FACE,{"disambiguationData":[OSD([sQuery(id+"F4.wireOp",EDGE,"E30")])]}),makeQuery(id+"F8.opExtrude","SWEPT_FACE",FACE,{"disambiguationData":[OSD([sQuery(id+"F7.wireOp",EDGE,"E67")])]})]});
            fillet(context, id + "F14", {"entities" : qUnion([Q0, Q1, Q2, Q3, Q4, Q5]), "radius" : 3 * mm, "tangentPropagation" : true, "allowEdgeOverflow" : false});
        }
        {
            var Q0;
            Q0=makeQuery(id+"F1.opExtrude","CAP_EDGE",EDGE,{"disambiguationData":[OSD([sQuery(id+"F0.wireOp",EDGE,"E1.bottom")])],"isStart":false});
            fillet(context, id + "F15", {"entities" : qUnion([Q0]), "radius" : 2 * mm, "tangentPropagation" : true, "allowEdgeOverflow" : false});
        }
        {
            var Q0;
            {var subQ0=sQuery(id+"F0.wireOp",EDGE,"E21.filletArc");var subQ1=sQuery(id+"F0.wireOp",EDGE,"E7");var subQ2=sQuery(id+"F0.wireOp",EDGE,"E6");var subQ3=sQuery(id+"F0.wireOp",EDGE,"E5");var subQ4=sQuery(id+"F0.wireOp",EDGE,"E4");var subQ5=sQuery(id+"F0.wireOp",EDGE,"E22.filletArc");var subQ6=sQuery(id+"F0.wireOp",EDGE,"E1.bottom");var subQ7=sQuery(id+"F0.wireOp",EDGE,"E1.right");var subQ8=sQuery(id+"F0.wireOp",EDGE,"E1.top");var subQ9=sQuery(id+"F0.wireOp",EDGE,"E1.left");var subQ10=sQuery(id+"F0.wireOp",EDGE,"E23.filletArc");var subQ11=sQuery(id+"F0.wireOp",EDGE,"E24.filletArc");Q0=makeQuery(id+"F2.boolean.opBoolean","SPLIT",FACE,{"disambiguationData":[TD([makeQuery(id+"F1.opExtrude","SWEPT_FACE",FACE,{"disambiguationData":[OSD([subQ6])]})])],"derivedFrom":makeQuery(id+"F1.opExtrude","CAP_FACE",FACE,{"disambiguationData":[OSD([subQ6,subQ8,subQ9,subQ7,subQ4,subQ3,subQ2,subQ1,subQ0,subQ5,subQ10,subQ11])],"isStart":true})});}
            var sketch = newSketch(context, id + "F16", { "sketchPlane" : qUnion([Q0])});
            skLineSegment(sketch, "E79", {"start": v(0, 90) * mm, "end": v(0, 120) * mm, "construction": true});
            skLineSegment(sketch, "E80", {"start": v(-15, 120) * mm, "end": v(-15, 108) * mm});
            skLineSegment(sketch, "E81", {"start": v(15, 120) * mm, "end": v(15, 108) * mm});
            skArc(sketch, "E82", {"start": v(15, 120) * mm, "mid": v(0, 135) * mm, "end": v(-15, 120) * mm});
            skLineSegment(sketch, "E83", {"start": v(-15, 108) * mm, "end": v(-33, 90) * mm});
            skLineSegment(sketch, "E84", {"start": v(15, 108) * mm, "end": v(33, 90) * mm});
            skCircle(sketch, "E85", {"center": v(0, 120) * mm, "radius": 6 * mm});
            skLineSegment(sketch, "E86", {"start": v(-80, 0) * mm, "end": v(80, 0) * mm, "construction": true});
            skArc(sketch, "E87.MirrorCS", {"start": v(15, -120) * mm, "mid": v(0, -135) * mm, "end": v(-15, -120) * mm});
            skLineSegment(sketch, "E88.MirrorCS", {"start": v(-15, -120) * mm, "end": v(-15, -108) * mm});
            skLineSegment(sketch, "E89.MirrorCS", {"start": v(15, -120) * mm, "end": v(15, -108) * mm});
            skCircle(sketch, "E90.MirrorC", {"center": v(0, -120) * mm, "radius": 6 * mm});
            skLineSegment(sketch, "E91.MirrorCS", {"start": v(0, -90) * mm, "end": v(0, -120) * mm, "construction": true});
            skLineSegment(sketch, "E92.MirrorCS", {"start": v(-15, -108) * mm, "end": v(-33, -90) * mm});
            skLineSegment(sketch, "E93.MirrorCS", {"start": v(15, -108) * mm, "end": v(33, -90) * mm});
            skSolve(sketch);
        }
        {
            var Q0;
            Q0=makeQuery(id+"F16.imprint","IMPRINT",FACE,{"disambiguationData":[TD([[makeQuery(id+"F16.imprint","IMPRINT",EDGE,{"derivedFrom":sQuery(id+"F16.wireOp",EDGE,"E80")}),1.0]])]});
            var Q1;
            Q1=makeQuery(id+"F16.imprint","IMPRINT",FACE,{"disambiguationData":[TD([[makeQuery(id+"F16.imprint","IMPRINT",EDGE,{"derivedFrom":makeQuery(id+"F1.opExtrude","CAP_EDGE",EDGE,{"disambiguationData":[OSD([sQuery(id+"F0.wireOp",EDGE,"E1.left")])],"isStart":true})}),-1.0]])]});
            var Q2;
            Q2=makeQuery(id+"F16.imprint","IMPRINT",FACE,{"disambiguationData":[TD([[makeQuery(id+"F16.imprint","IMPRINT",EDGE,{"derivedFrom":sQuery(id+"F16.wireOp",EDGE,"E87.MirrorCS")}),-1.0]])]});
            var Q3;
            Q3=makeQuery(id+"F2.opExtrude","CAP_FACE",FACE,{"disambiguationData":[OSD([sQuery(id+"F0.wireOp",EDGE,"E12"),sQuery(id+"F0.wireOp",EDGE,"E13"),sQuery(id+"F0.wireOp",EDGE,"E14"),sQuery(id+"F0.wireOp",EDGE,"E15"),sQuery(id+"F0.wireOp",EDGE,"E17.filletArc"),sQuery(id+"F0.wireOp",EDGE,"E18.filletArc"),sQuery(id+"F0.wireOp",EDGE,"E19.filletArc"),sQuery(id+"F0.wireOp",EDGE,"E20.filletArc"),sQuery(id+"F0.wireOp",EDGE,"E25.0"),sQuery(id+"F0.wireOp",EDGE,"E25.1"),sQuery(id+"F0.wireOp",EDGE,"E25.2"),sQuery(id+"F0.wireOp",EDGE,"E25.3"),sQuery(id+"F0.wireOp",EDGE,"E25.4"),sQuery(id+"F0.wireOp",EDGE,"E25.5"),sQuery(id+"F0.wireOp",EDGE,"E25.6"),sQuery(id+"F0.wireOp",EDGE,"E25.7")])],"isStart":false});
            extrude(context, id + "F17", {"entities" : qUnion([Q0, Q1, Q2]), "endBound" : BoundingType.UP_TO_SURFACE, "endBoundEntityFace" : qUnion([Q3]), "depth" : 25 * mm});
        }
    });
